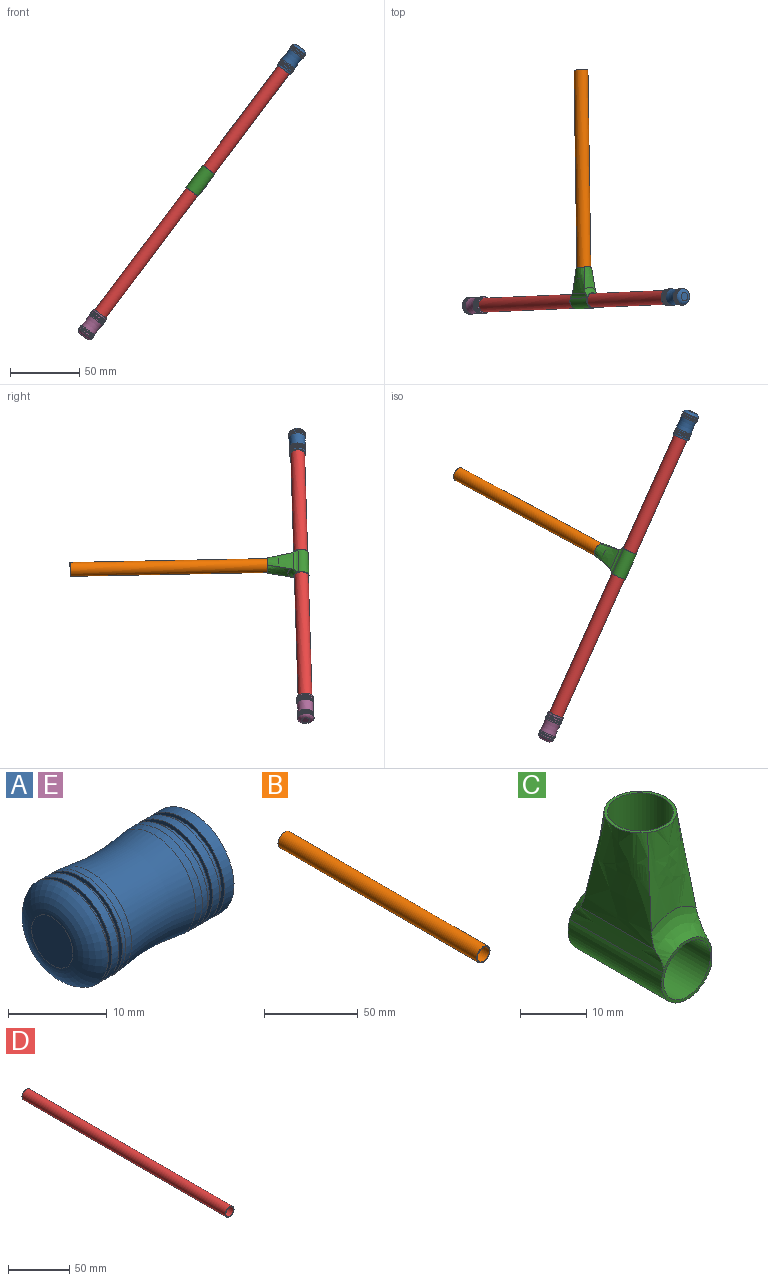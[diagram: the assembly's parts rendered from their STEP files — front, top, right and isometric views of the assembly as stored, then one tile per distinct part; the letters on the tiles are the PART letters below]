
ASSEMBLY  parts=5 mates=4
PART A: 25 faces, bbox 36.6x28.1x28.1 mm
  f0: cylinder r=5.51mm len=11.03mm, axis (1,0,0), area 18mm2, adj f1,f21
  f1: plane 12x12mm, normal (1,0,0), area 17.6mm2, adj f0,f22
  f2: plane 5.92x5.92mm, normal (-1,0,0), area 27.6mm2, adj f22
  f3: plane 10x10mm, normal (1,0,0), area 78.5mm2, adj f4
  f4: cylinder r=5mm len=18mm, axis (1,0,0), area 565.5mm2, adj f3,f5
  f5: plane 12x12mm, normal (1,0,0), area 34.6mm2, adj f4,f6
  f6: cylinder r=6mm len=12mm, axis (1,0,0), area 51.7mm2, adj f5,f7
  f7: plane 12x12mm, normal (-1,0,0), area 17.2mm2, adj f6,f8
  f8: cylinder r=5.53mm len=11.05mm, axis (1,0,0), area 24.3mm2, adj f7,f9
  f9: plane 12x12mm, normal (1,0,0), area 17.2mm2, adj f8,f10
  f10: cylinder r=6mm len=12mm, axis (1,0,0), area 37.3mm2, adj f9,f11
  f11: plane 12x12mm, normal (-1,0,0), area 17.2mm2, adj f10,f12
  f12: cylinder r=5.53mm len=11.05mm, axis (1,0,0), area 24.3mm2, adj f11,f13
  f13: plane 12x12mm, normal (1,0,0), area 17.2mm2, adj f12,f14
  f14: cylinder r=6mm len=12mm, axis (1,0,0), area 28.8mm2, adj f13,f23
  f15: torus R=31.29mm, axis (1,0,0), area 326.3mm2, adj f23,f24
  f16: cylinder r=6mm len=12mm, axis (1,0,0), area 18.5mm2, adj f17,f24
  f17: plane 12x12mm, normal (-1,0,0), area 17.6mm2, adj f16,f18
  f18: cylinder r=5.51mm len=11.03mm, axis (1,0,0), area 17.8mm2, adj f17,f19
  f19: plane 12x12mm, normal (1,0,0), area 17.6mm2, adj f18,f20
  f20: cylinder r=6mm len=12mm, axis (1,0,0), area 37.7mm2, adj f19,f21
  f21: plane 12x12mm, normal (-1,0,0), area 17.6mm2, adj f0,f20
  f22: torus R=2.96mm, axis (-1,0,0), area 113.2mm2, adj f1,f2
  f23: torus R=0.92mm, axis (-1,0,0), area 34mm2, adj f14,f15
  f24: torus R=0.92mm, axis (-1,0,0), area 34mm2, adj f15,f16
PART B: 4 faces, bbox 10x150x10 mm
  f0: cylinder r=4.5mm len=150mm, axis (0,1,0), area 4241.2mm2, adj f2,f3
  f1: cylinder r=5mm len=150mm, axis (0,1,0), area 4712.4mm2, adj f2,f3
  f2: plane 10x10mm, normal (0,-1,0), area 14.9mm2, adj f0,f1
  f3: plane 10x10mm, normal (0,1,0), area 14.9mm2, adj f0,f1
PART C: 18 faces, bbox 18.5x23.9x29.9 mm
  f0: cylinder r=5.5mm len=20mm, axis (0,-1,0), area 359.5mm2, adj f2,f4,f10,f14
  f1: cylinder r=5mm len=20mm, axis (0,-1,0), area 625.2mm2, adj f2,f4,f17
  f2: plane 11.14x10.98mm, normal (0,1,0), area 16.2mm2, adj f0,f1,f3,f12,f14
  f3: cylinder r=5.5mm len=20mm, axis (0,-1,0), area 14mm2, adj f2,f4,f11,f14
  f4: plane 11.14x10.98mm, normal (0,-1,0), area 16.2mm2, adj f0,f1,f3,f13,f14
  f5: bspline ~19.05x10.11mm, area 150.9mm2, adj f7,f8,f9,f12
  f6: bspline ~19.05x10.11mm, area 150.9mm2, adj f7,f8,f9,f13
  f7: plane 11x11mm, normal (0,0,1), area 16.5mm2, adj f5,f6,f8,f9,f15
  f8: bspline ~19.05x16.12mm, area 222.3mm2, adj f5,f6,f7,f10,f12,f13
  f9: bspline ~19.05x16.12mm, area 222.3mm2, adj f5,f6,f7,f11,f12,f13
  f10: bspline ~23.71x3.27mm, area 59.9mm2, adj f0,f8,f12,f13
  f11: bspline ~23.71x3.27mm, area 59.9mm2, adj f3,f9,f12,f13
  f12: bspline ~18.25x8.03mm, area 59.3mm2, adj f2,f5,f8,f9,f10,f11
  f13: bspline ~18.25x8.03mm, area 59.3mm2, adj f4,f6,f8,f9,f10,f11
  f14: plane 20x2.63mm, normal (1,0,0), area 49.4mm2, adj f0,f2,f3,f4,f17
  f15: cylinder r=5mm len=10mm, axis (0,0,1), area 251.3mm2, adj f7,f16
  f16: plane 10x10mm, normal (0,0,1), area 78.5mm2, adj f15
  f17: cylinder r=1mm len=2mm, axis (1,0,0), area 2.8mm2, adj f1,f14
PART D: 4 faces, bbox 10x235x10 mm
  f0: cylinder r=4.5mm len=235mm, axis (0,1,0), area 6644.5mm2, adj f2,f3
  f1: cylinder r=5mm len=235mm, axis (0,1,0), area 7382.7mm2, adj f2,f3
  f2: plane 10x10mm, normal (0,-1,0), area 14.9mm2, adj f0,f1
  f3: plane 10x10mm, normal (0,1,0), area 14.9mm2, adj f0,f1
PART E: same geometry as A
PLACE A rot(axis=(-0.01,1,-0.01),127deg) t=(44.67,-93.23,107.49)mm
PLACE B rot(axis=(-0.04,1,0.01),37deg) t=(-22.76,-4.63,17.84)mm
PLACE C rot(axis=(-0.91,0.3,0.3),97deg) t=(-21.51,-90.66,19.51)mm
PLACE D rot(axis=(-0.41,-0.4,0.82),102.6deg) t=(-57.48,-97.36,-28.33)mm
PLACE E rot(axis=(0.89,0.01,0.45),179.4deg) t=(-99.54,-99.06,-84.26)mm
MATE fastened D.f0 <-> C.f0  axis (0.6,0.02,0.8) through (38.66,-93.47,99.5)mm
MATE fastened E.f0 <-> D.f0  axis (0.6,0.02,0.8) through (-93.54,-98.82,-76.27)mm
MATE fastened A.f0 <-> D.f1  axis (-0.6,-0.02,-0.8) through (38.66,-93.47,99.5)mm
MATE fastened C.f15 <-> B.f1  axis (-0.01,1,-0.02) through (-21.67,-79.61,19.29)mm
